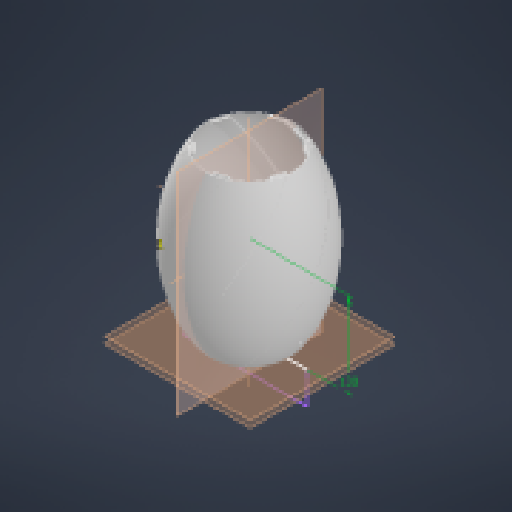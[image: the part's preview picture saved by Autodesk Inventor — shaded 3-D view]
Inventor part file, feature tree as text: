
AUTODESK INVENTOR PART (.ipt)
format: ipt  version: 2023 (Build 270158000, 158)  size: 4,650,496 bytes
history: native  units: mm
features: sketch x13, extrude x8, projected_geometry x6, plane x5, other x5, pattern_circular x4, revolve x2, sweep x1, chamfer x1, shell x1, reference x1
ambient origin geometry x8: Origin, YZ Plane, XZ Plane, XY Plane, X Axis, Y Axis, Z Axis, Center Point
bodies: Solid1 (feature_tree)
feature tree (47):
  revolve  "Revolution1"  [1 undecoded]
  sketch  "3D Sketch1"
  plane  "Work Plane1"
  sweep  "Sweep1"
  pattern_circular  "Circular Pattern1"  Count=6 Angle=360.0deg
  extrude  "Extrusion1"  TaperAngle=0.0deg  [1 undecoded]
  plane  "Work Plane3"
  sketch  "Sketch12"  dims[d16=0.2mm]
  plane  "Work Plane6"
  extrude  "Extrusion6"  Depth=1.0mm
  chamfer  "Chamfer2"  Distance=10.0mm
  pattern_circular  "Circular Pattern4"  [2 undecoded]
  shell  "Shell2"  Thickness=4.0mm
  sketch  "Sketch16"  dims[d26=-130.0mm d27=-10.0mm d29=1.0mm d30=10.0mm d31=0.0mm d32=6.0mm d33=4.0mm d34=0.0mm d35=4.0mm d36=4.0mm d37=0.0mm d38=30.0mm d39=360.0deg d51=100.0mm d52=6.0mm d53=4.0mm d54=0.0mm d55=3.5mm d56=1.0mm d57=45.0deg d58=30.0mm d59=360.0deg d61=30.0deg d62=6.0mm d63=4.0mm d64=0.0mm d65=60.0mm d66=360.0deg d68=360.0deg d69=130.0mm d70=0.0mm d71=0.0mm d72=0.0mm d73=0.0mm]
  extrude  "Extrusion8"  Depth=4.0mm
  extrude  "Extrusion2"  Depth=4.0mm TaperAngle=0.0deg
  sketch  "Sketch7"  dims[d13=1.6mm]
  plane  "Work Plane4"
  extrude  "Extrusion3"  Depth=30.0mm TaperAngle=360.0deg
  extrude  "Extrusion4"  Depth=100.0mm
  pattern_circular  "Circular Pattern2"  [2 undecoded]
  extrude  "Extrusion7"  Depth=4.0mm TaperAngle=0.0deg
  pattern_circular  "Circular Pattern5"  Angle=45.0deg  [1 undecoded]
  revolve  "Revolution2"  Angle=360.0deg
  extrude  "Extrusion9"  TaperAngle=30.0deg  [1 undecoded]
  sketch  "Sketch1"  dims[d0=160.0mm d1=100.0mm]
  other  "Helical Curve2"
  other  "Project to Surface1"
  sketch  "Sketch2"  dims[d2=90.0deg d7=1200.0mm d8=637.649mm d9=252.623mm d10=0.0mm]
  sketch  "Sketch3"  dims[d11=15.0mm]
  plane  "Work Plane2"
  sketch  "Sketch6"  dims[d12=3.0mm]
  sketch  "Sketch8"  dims[d14=1.478932mm]
  sketch  "Sketch9"  dims[d15=0.2mm]
  sketch  "Sketch13"  dims[d17=0.2mm]
  sketch  "Sketch14"  dims[d18=0.0mm d19=0.0mm d20=60.0mm d21=360.0deg]
  reference  "Reference1"
  sketch  "Sketch15"  dims[d23=120.0mm d24=0.0mm d25=0.0mm]
  projected_geometry  "Project Cut Edges1"
  projected_geometry  "Project Cut Edges2"
  projected_geometry  "Project Cut Edges3"
  projected_geometry  "Project Cut Edges5"
  projected_geometry  "Project Cut Edges6"
  parser-record x1  (decoder bookkeeping rows leaked as tree rows — omitted from the tree; the rows remain in map.json)
  other  "assembly.iam"
  other  "ring_unten:1"
  projected_geometry  "Project Cut Edges7"
note: 8 required parameter values undecoded (feature->parameter linkage not recoverable at this tier; creation-order binding heuristic only, values carry confidence <= 0.55)
note: 1 file-system path scrubbed to <path> (originals preserved in map.json)